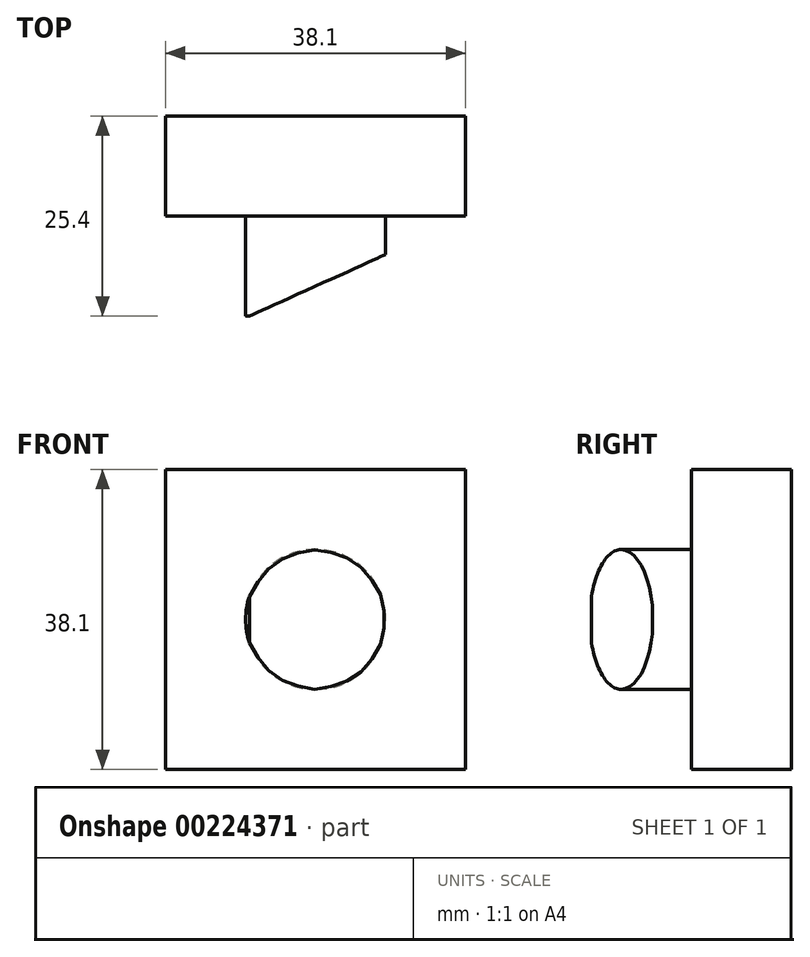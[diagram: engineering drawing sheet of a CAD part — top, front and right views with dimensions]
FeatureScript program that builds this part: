
annotation { "Feature Type Name" : "Feature", "Feature Type Description" : "" }
export const myFeature = defineFeature(function(context is Context, id is Id, definition is map)
    precondition{}
    {
        {
            var Q0;
            Q0=qCreatedBy(makeId("Front.planeOp"),FACE);
            var sketch = newSketch(context, id + "F0", { "sketchPlane" : qUnion([Q0])});
            skLineSegment(sketch, "E0", {"start": v(0, 0) * mm, "end": v(0, 38.1) * mm});
            skLineSegment(sketch, "E1", {"start": v(0, 38.1) * mm, "end": v(38.1, 38.1) * mm});
            skLineSegment(sketch, "E2", {"start": v(38.1, 38.1) * mm, "end": v(38.1, 0) * mm});
            skLineSegment(sketch, "E3", {"start": v(38.1, 0) * mm, "end": v(0, 0) * mm});
            skSolve(sketch);
        }
        {
            var Q0;
            Q0=makeQuery(id+"F0.imprint","IMPRINT",FACE,{"disambiguationData":[TD([[makeQuery(id+"F0.imprint","IMPRINT",EDGE,{"derivedFrom":sQuery(id+"F0.wireOp",EDGE,"E0")}),-1.0]])]});
            extrude(context, id + "F1", {"entities" : qUnion([Q0]), "depth" : 12.7 * mm});
        }
        {
            var Q0;
            Q0=makeQuery(id+"F1.opExtrude","CAP_FACE",FACE,{"disambiguationData":[OSD([sQuery(id+"F0.wireOp",EDGE,"E0"),sQuery(id+"F0.wireOp",EDGE,"E1"),sQuery(id+"F0.wireOp",EDGE,"E2"),sQuery(id+"F0.wireOp",EDGE,"E3")])],"isStart":false});
            var sketch = newSketch(context, id + "F2", { "sketchPlane" : qUnion([Q0])});
            skCircle(sketch, "E4", {"center": v(19.05, 19.05) * mm, "radius": 8.9 * mm});
            skSolve(sketch);
        }
        {
            var Q0;
            Q0 = qSketchRegion(id + "F2", true);
            extrude(context, id + "F3", {"entities" : qUnion([Q0]), "operationType" : NewBodyOperationType.ADD, "depth" : 12.7 * mm});
        }
        {
            var Q0;
            Q0=qCreatedBy(makeId("Top.planeOp"),FACE);
            var sketch = newSketch(context, id + "F4", { "sketchPlane" : qUnion([Q0])});
            skLineSegment(sketch, "E5", {"start": v(9, -26.15) * mm, "end": v(29.38, -16.94) * mm});
            skLineSegment(sketch, "E6", {"start": v(29.38, -16.94) * mm, "end": v(29.38, -26.15) * mm});
            skLineSegment(sketch, "E7", {"start": v(29.38, -26.15) * mm, "end": v(9, -26.15) * mm});
            skSolve(sketch);
        }
        {
            var Q0;
            Q0=makeQuery(id+"F4.imprint","IMPRINT",FACE,{"disambiguationData":[TD([[makeQuery(id+"F4.imprint","IMPRINT",EDGE,{"derivedFrom":sQuery(id+"F4.wireOp",EDGE,"E5")}),-1.0]])]});
            extrude(context, id + "F5", {"entities" : qUnion([Q0]), "operationType" : NewBodyOperationType.REMOVE, "depth" : 254 * mm});
        }
    });
